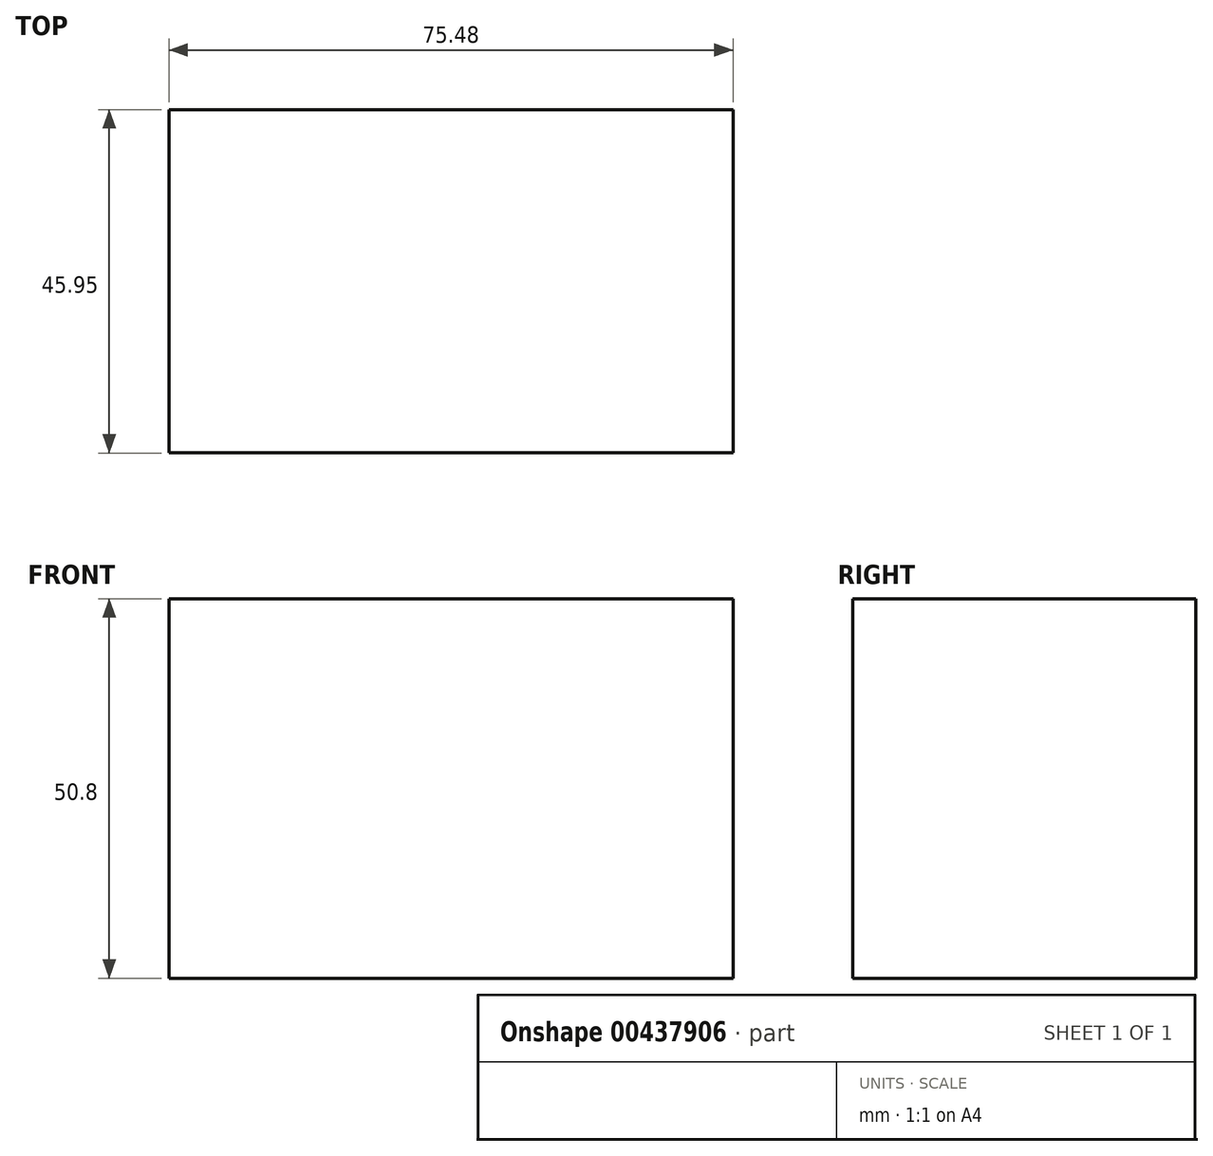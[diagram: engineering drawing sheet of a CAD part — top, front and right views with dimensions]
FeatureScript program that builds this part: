
annotation { "Feature Type Name" : "Feature", "Feature Type Description" : "" }
export const myFeature = defineFeature(function(context is Context, id is Id, definition is map)
    precondition{}
    {
        {
            var Q0;
            Q0=qCreatedBy(makeId("Top.planeOp"),FACE);
            var sketch = newSketch(context, id + "F0", { "sketchPlane" : qUnion([Q0])});
            skLineSegment(sketch, "E0.bottom", {"start": v(0, 0) * mm, "end": v(75.48, 0) * mm});
            skLineSegment(sketch, "E0.top", {"start": v(0, -45.95) * mm, "end": v(75.48, -45.95) * mm});
            skLineSegment(sketch, "E0.left", {"start": v(0, 0) * mm, "end": v(0, -45.95) * mm});
            skLineSegment(sketch, "E0.right", {"start": v(75.48, 0) * mm, "end": v(75.48, -45.95) * mm});
            skSolve(sketch);
        }
        {
            var Q0;
            Q0 = qSketchRegion(id + "F0", true);
            extrude(context, id + "F1", {"entities" : qUnion([Q0]), "depth" : 50.8 * mm});
        }
    });
